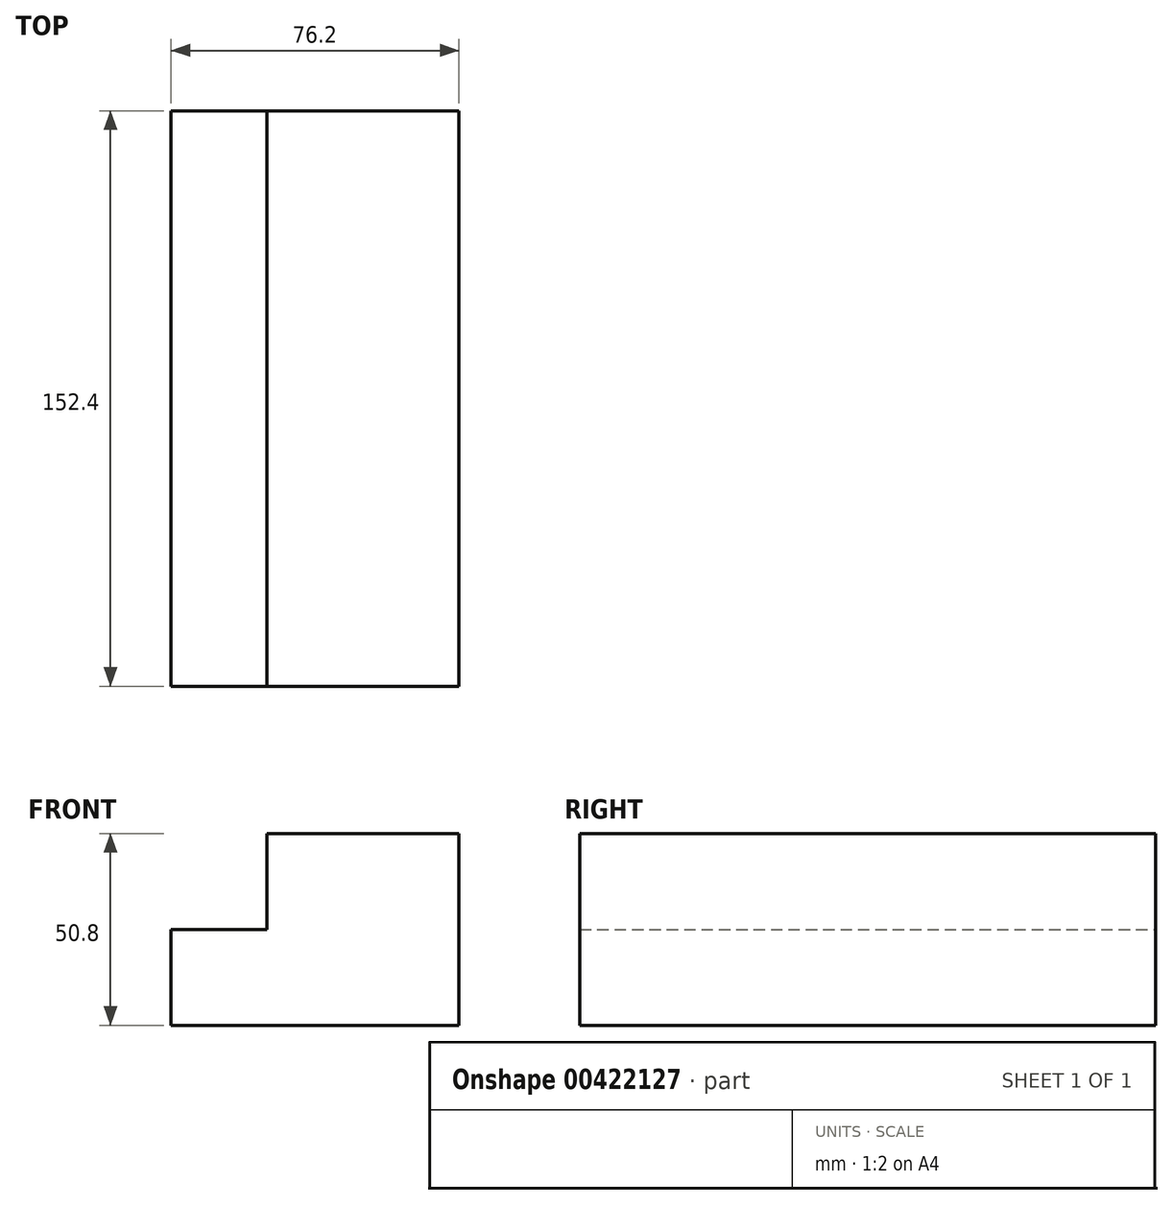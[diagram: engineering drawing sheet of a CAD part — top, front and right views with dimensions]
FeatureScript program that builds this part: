
annotation { "Feature Type Name" : "Feature", "Feature Type Description" : "" }
export const myFeature = defineFeature(function(context is Context, id is Id, definition is map)
    precondition{}
    {
        {
            var Q0;
            Q0=qCreatedBy(makeId("Front.planeOp"),FACE);
            var sketch = newSketch(context, id + "F0", { "sketchPlane" : qUnion([Q0])});
            skLineSegment(sketch, "E0", {"start": v(0, 0) * mm, "end": v(76.2, 0) * mm});
            skLineSegment(sketch, "E1", {"start": v(76.2, 0) * mm, "end": v(76.2, 50.8) * mm});
            skLineSegment(sketch, "E2", {"start": v(76.2, 50.8) * mm, "end": v(25.4, 50.8) * mm});
            skLineSegment(sketch, "E3", {"start": v(25.4, 50.8) * mm, "end": v(25.4, 25.4) * mm});
            skLineSegment(sketch, "E4", {"start": v(25.4, 25.4) * mm, "end": v(0, 25.4) * mm});
            skLineSegment(sketch, "E5", {"start": v(0, 25.4) * mm, "end": v(0, 0) * mm});
            skSolve(sketch);
        }
        {
            var Q0;
            Q0=makeQuery(id+"F0.imprint","IMPRINT",FACE,{"disambiguationData":[TD([[makeQuery(id+"F0.imprint","IMPRINT",EDGE,{"derivedFrom":sQuery(id+"F0.wireOp",EDGE,"E0")}),1.0]])]});
            extrude(context, id + "F1", {"entities" : qUnion([Q0]), "depth" : 152.4 * mm});
        }
    });
